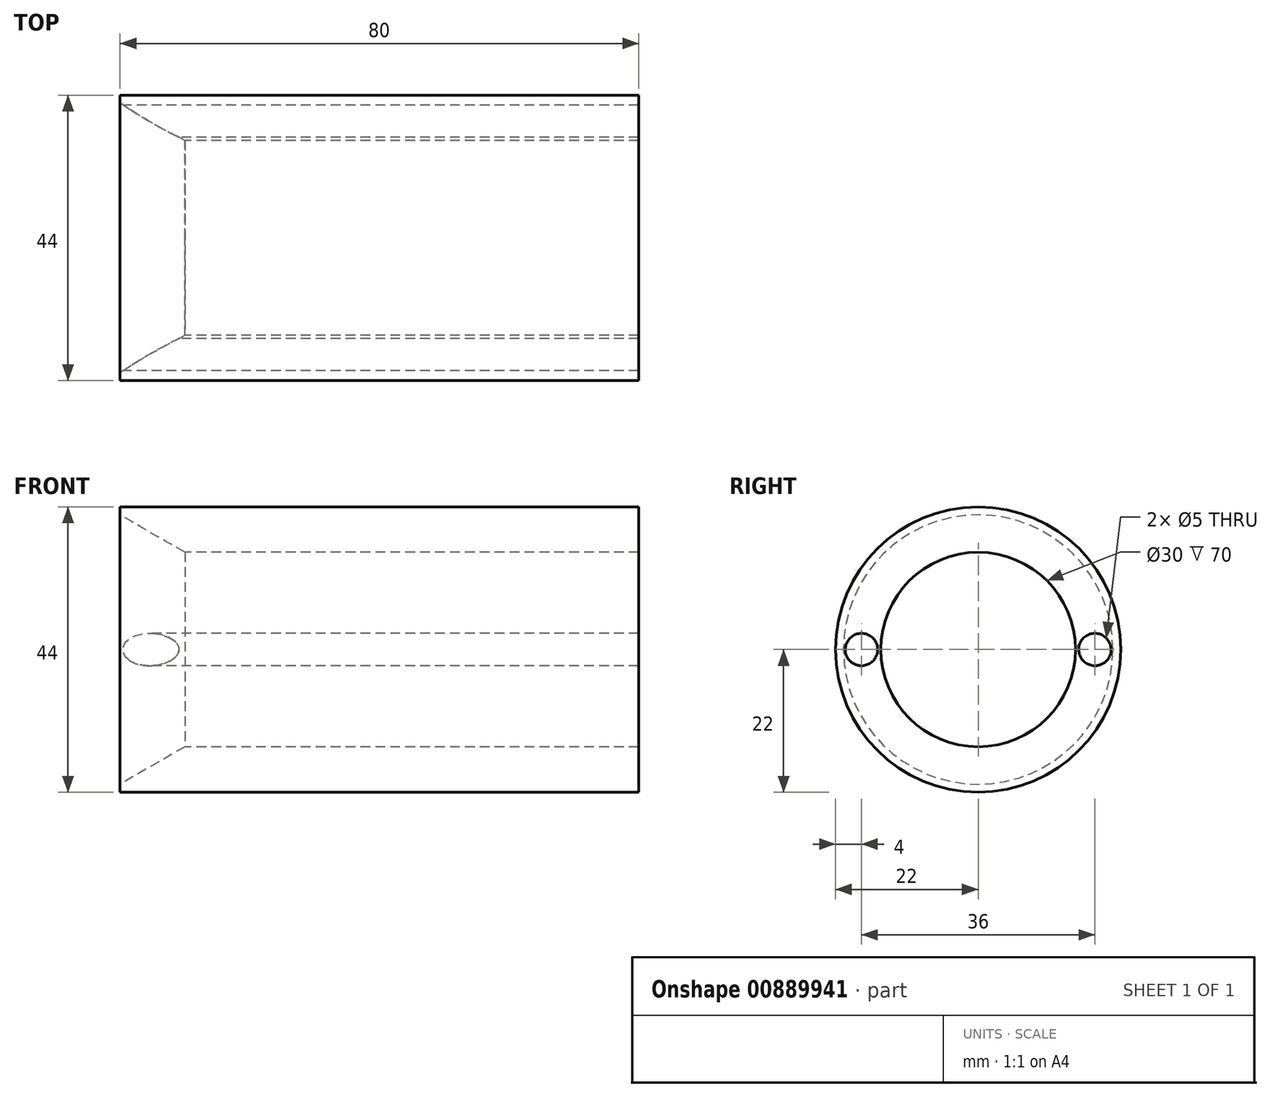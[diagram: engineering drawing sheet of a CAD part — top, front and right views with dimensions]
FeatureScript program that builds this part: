
annotation { "Feature Type Name" : "Feature", "Feature Type Description" : "" }
export const myFeature = defineFeature(function(context is Context, id is Id, definition is map)
    precondition{}
    {
        {
            var Q0;
            Q0=qCreatedBy(makeId("Front.planeOp"),FACE);
            var sketch = newSketch(context, id + "F0", { "sketchPlane" : qUnion([Q0])});
            skLineSegment(sketch, "E0", {"start": v(0, 22) * mm, "end": v(0, 20.77) * mm});
            skLineSegment(sketch, "E1", {"start": v(0, 20.77) * mm, "end": v(10, 15) * mm});
            skLineSegment(sketch, "E2", {"start": v(0, 22) * mm, "end": v(80, 22) * mm});
            skLineSegment(sketch, "E3", {"start": v(80, 22) * mm, "end": v(80, 15) * mm});
            skLineSegment(sketch, "E4", {"start": v(80, 15) * mm, "end": v(10, 15) * mm});
            skLineSegment(sketch, "E5", {"start": v(0, 0) * mm, "end": v(163.75, 0) * mm});
            skSolve(sketch);
        }
        {
            var Q0;
            Q0=makeQuery(id+"F0.imprint","IMPRINT",FACE,{"disambiguationData":[TD([[makeQuery(id+"F0.imprint","IMPRINT",EDGE,{"derivedFrom":sQuery(id+"F0.wireOp",EDGE,"E0")}),1.0]])]});
            var Q1;
            Q1=sQuery(id+"F0.wireOp",EDGE,"E5");
            revolve(context, id + "F1", {"surfaceOperationType" : NewSurfaceOperationType.NEW, "entities" : qUnion([Q0]), "axis" : qUnion([Q1]), "revolveType" : RevolveType.FULL});
        }
        {
            var Q0;
            Q0=qCreatedBy(makeId("Right.planeOp"),FACE);
            var sketch = newSketch(context, id + "F2", { "sketchPlane" : qUnion([Q0])});
            skCircle(sketch, "E6", {"center": v(18, 0) * mm, "radius": 2.5 * mm});
            skCircle(sketch, "E7", {"center": v(-18, 0) * mm, "radius": 2.5 * mm});
            skSolve(sketch);
        }
        {
            var Q0;
            Q0 = qSketchRegion(id + "F2", true);
            extrude(context, id + "F3", {"entities" : qUnion([Q0]), "operationType" : NewBodyOperationType.REMOVE, "endBound" : BoundingType.THROUGH_ALL, "depth" : 25 * mm, "offsetDistance" : 25 * mm});
        }
    });
